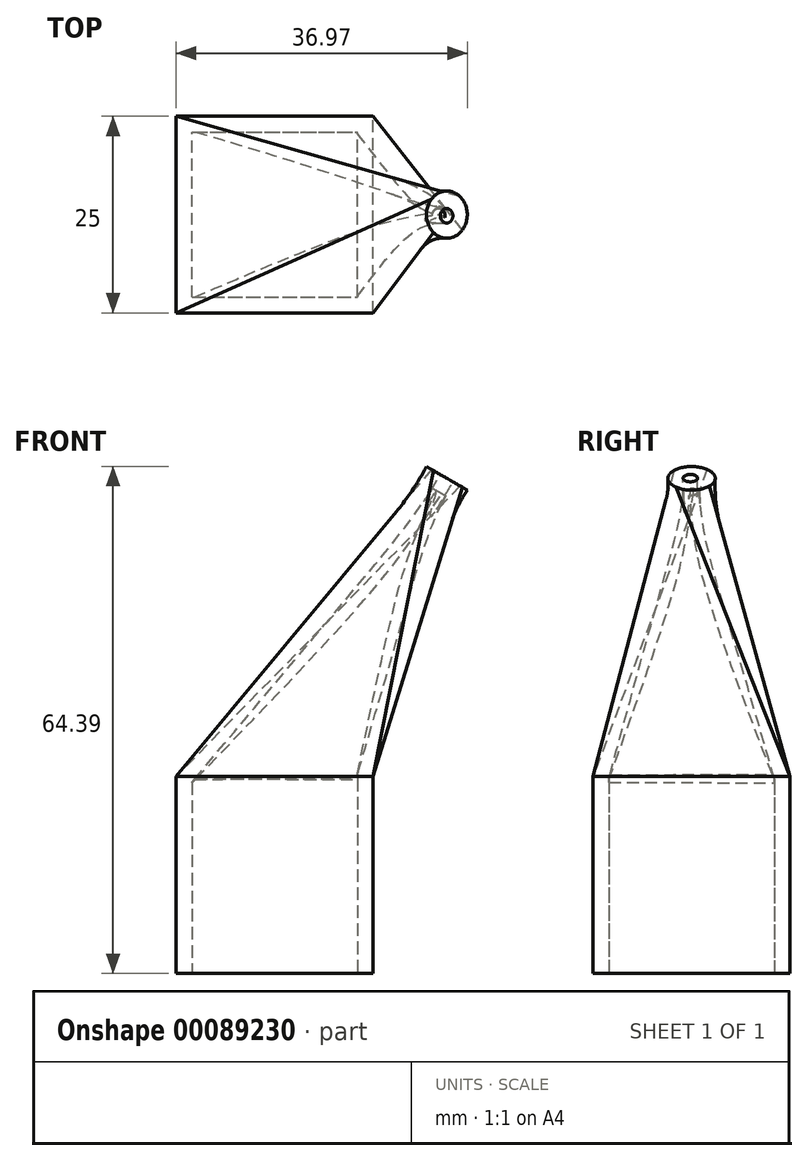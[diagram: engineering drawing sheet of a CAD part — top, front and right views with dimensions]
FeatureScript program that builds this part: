
annotation { "Feature Type Name" : "Feature", "Feature Type Description" : "" }
export const myFeature = defineFeature(function(context is Context, id is Id, definition is map)
    precondition{}
    {
        {
            var Q0;
            Q0=qCreatedBy(makeId("Top.planeOp"),FACE);
            var sketch = newSketch(context, id + "F0", { "sketchPlane" : qUnion([Q0])});
            skLineSegment(sketch, "E0.bottom", {"start": v(0, 0) * mm, "end": v(25, 0) * mm});
            skLineSegment(sketch, "E0.top", {"start": v(0, 25) * mm, "end": v(25, 25) * mm});
            skLineSegment(sketch, "E0.left", {"start": v(0, 0) * mm, "end": v(0, 25) * mm});
            skLineSegment(sketch, "E0.right", {"start": v(25, 0) * mm, "end": v(25, 25) * mm});
            skSolve(sketch);
        }
        {
            var Q0;
            Q0=makeQuery(id+"F0.imprint","IMPRINT",FACE,{"disambiguationData":[TD([[makeQuery(id+"F0.imprint","IMPRINT",EDGE,{"derivedFrom":sQuery(id+"F0.wireOp",EDGE,"E0.bottom")}),1.0]])]});
            extrude(context, id + "F1", {"entities" : qUnion([Q0]), "depth" : 25 * mm});
        }
        {
            var Q0;
            Q0=makeQuery(id+"F1.opExtrude","CAP_FACE",FACE,{"disambiguationData":[OSD([sQuery(id+"F0.wireOp",EDGE,"E0.bottom"),sQuery(id+"F0.wireOp",EDGE,"E0.top"),sQuery(id+"F0.wireOp",EDGE,"E0.left"),sQuery(id+"F0.wireOp",EDGE,"E0.right")])],"isStart":false});
            var Q1;
            Q1=makeQuery(id+"F1.opExtrude","CAP_EDGE",EDGE,{"disambiguationData":[OSD([sQuery(id+"F0.wireOp",EDGE,"E0.left")])],"isStart":false});
            cPlane(context, id + "F2", {"entities" : qUnion([Q0, Q1]), "cplaneType" : CPlaneType.LINE_ANGLE, "offset" : 150 * mm, "angle" : 30 * degree, "width" : 150 * mm, "height" : 150 * mm});
        }
        {
            var Q0;
            Q0=qCreatedBy(id+"F2.planeOp",FACE);
            cPlane(context, id + "F3", {"entities" : qUnion([Q0]), "cplaneType" : CPlaneType.OFFSET, "offset" : 50 * mm, "oppositeDirection" : true, "width" : 150 * mm, "height" : 150 * mm});
        }
        {
            var Q0;
            Q0=qCreatedBy(id+"F3.planeOp",FACE);
            var sketch = newSketch(context, id + "F4", { "sketchPlane" : qUnion([Q0])});
            skLineSegment(sketch, "E1.0.0", {"start": v(0, 0) * mm, "end": v(21.65, 0) * mm, "construction": true});
            skLineSegment(sketch, "E1.0.1", {"start": v(21.65, 0) * mm, "end": v(9.15, 0) * mm, "construction": true});
            skLineSegment(sketch, "E1.0.2", {"start": v(9.15, 0) * mm, "end": v(-12.5, 0) * mm, "construction": true});
            skLineSegment(sketch, "E1.0.3", {"start": v(-12.5, 0) * mm, "end": v(0, 0) * mm, "construction": true});
            skLineSegment(sketch, "E2.0.0", {"start": v(21.65, -25) * mm, "end": v(0, -25) * mm, "construction": true});
            skLineSegment(sketch, "E2.0.1", {"start": v(0, -25) * mm, "end": v(-12.5, -25) * mm, "construction": true});
            skLineSegment(sketch, "E2.0.2", {"start": v(-12.5, -25) * mm, "end": v(9.15, -25) * mm, "construction": true});
            skLineSegment(sketch, "E2.0.3", {"start": v(9.15, -25) * mm, "end": v(21.65, -25) * mm, "construction": true});
            skLineSegment(sketch, "E3.0", {"start": v(-12.5, 0) * mm, "end": v(-12.5, -25) * mm, "construction": true});
            skLineSegment(sketch, "E4", {"start": v(9.15, 0) * mm, "end": v(9.15, -25) * mm, "construction": true});
            skLineSegment(sketch, "E5", {"start": v(-12.5, 0) * mm, "end": v(9.15, -25) * mm, "construction": true});
            skCircle(sketch, "E6", {"center": v(-1.67, -12.5) * mm, "radius": 3 * mm});
            skSolve(sketch);
        }
        {
            var Q0;
            Q0=makeQuery(id+"F1.opExtrude","CAP_FACE",FACE,{"disambiguationData":[OSD([sQuery(id+"F0.wireOp",EDGE,"E0.bottom"),sQuery(id+"F0.wireOp",EDGE,"E0.top"),sQuery(id+"F0.wireOp",EDGE,"E0.left"),sQuery(id+"F0.wireOp",EDGE,"E0.right")])],"isStart":false});
            var sketch = newSketch(context, id + "F5", { "sketchPlane" : qUnion([Q0])});
            skLineSegment(sketch, "E7.bottom", {"start": v(0, 0) * mm, "end": v(25, 0) * mm});
            skLineSegment(sketch, "E7.top", {"start": v(0, 25) * mm, "end": v(25, 25) * mm});
            skLineSegment(sketch, "E7.left", {"start": v(0, 0) * mm, "end": v(0, 25) * mm});
            skLineSegment(sketch, "E7.right", {"start": v(25, 0) * mm, "end": v(25, 25) * mm});
            skSolve(sketch);
        }
        {
            var Q1;
            Q1=makeQuery(id+"F4.imprint","IMPRINT",FACE,{"disambiguationData":[TD([[makeQuery(id+"F4.imprint","IMPRINT",EDGE,{"derivedFrom":sQuery(id+"F4.wireOp",EDGE,"E6")}),1.0]])]});
            var Q2;
            Q2=makeQuery(id+"F5.imprint","IMPRINT",FACE,{"disambiguationData":[TD([[makeQuery(id+"F5.imprint","IMPRINT",EDGE,{"derivedFrom":sQuery(id+"F5.wireOp",EDGE,"E7.bottom")}),1.0]])]});
            loft(context, id + "F6", {"operationType" : NewBodyOperationType.ADD, "sheetProfilesArray" : [{ "sheetProfileEntities" : qUnion([Q1]) }, { "sheetProfileEntities" : qUnion([Q2]) }]});
        }
        {
            var Q0;
            Q0=makeQuery(id+"F1.opExtrude","CAP_FACE",FACE,{"disambiguationData":[OSD([sQuery(id+"F0.wireOp",EDGE,"E0.bottom"),sQuery(id+"F0.wireOp",EDGE,"E0.top"),sQuery(id+"F0.wireOp",EDGE,"E0.left"),sQuery(id+"F0.wireOp",EDGE,"E0.right")])],"isStart":true});
            shell(context, id + "F7", {"entities" : qUnion([Q0]), "thickness" : 2 * mm});
        }
        {
            var Q0;
            Q0=makeQuery(id+"F6.opLoft","CAP_FACE",FACE,{"disambiguationData":[OSD([makeQuery(id+"F4.imprint","IMPRINT",FACE,{"disambiguationData":[TD([[makeQuery(id+"F4.imprint","IMPRINT",EDGE,{"derivedFrom":sQuery(id+"F4.wireOp",EDGE,"E6")}),1.0]])]})])],"isStart":true});
            var sketch = newSketch(context, id + "F8", { "sketchPlane" : qUnion([Q0])});
            skCircle(sketch, "E8", {"center": v(-1.7, 12.34) * mm, "radius": 0.92 * mm});
            skSolve(sketch);
        }
        {
            var Q0;
            Q0=makeQuery(id+"F8.imprint","IMPRINT",FACE,{"disambiguationData":[TD([[makeQuery(id+"F8.imprint","IMPRINT",EDGE,{"derivedFrom":sQuery(id+"F8.wireOp",EDGE,"E8")}),1.0]])]});
            extrude(context, id + "F9", {"entities" : qUnion([Q0]), "operationType" : NewBodyOperationType.REMOVE, "oppositeDirection" : true, "depth" : 25 * mm});
        }
    });
